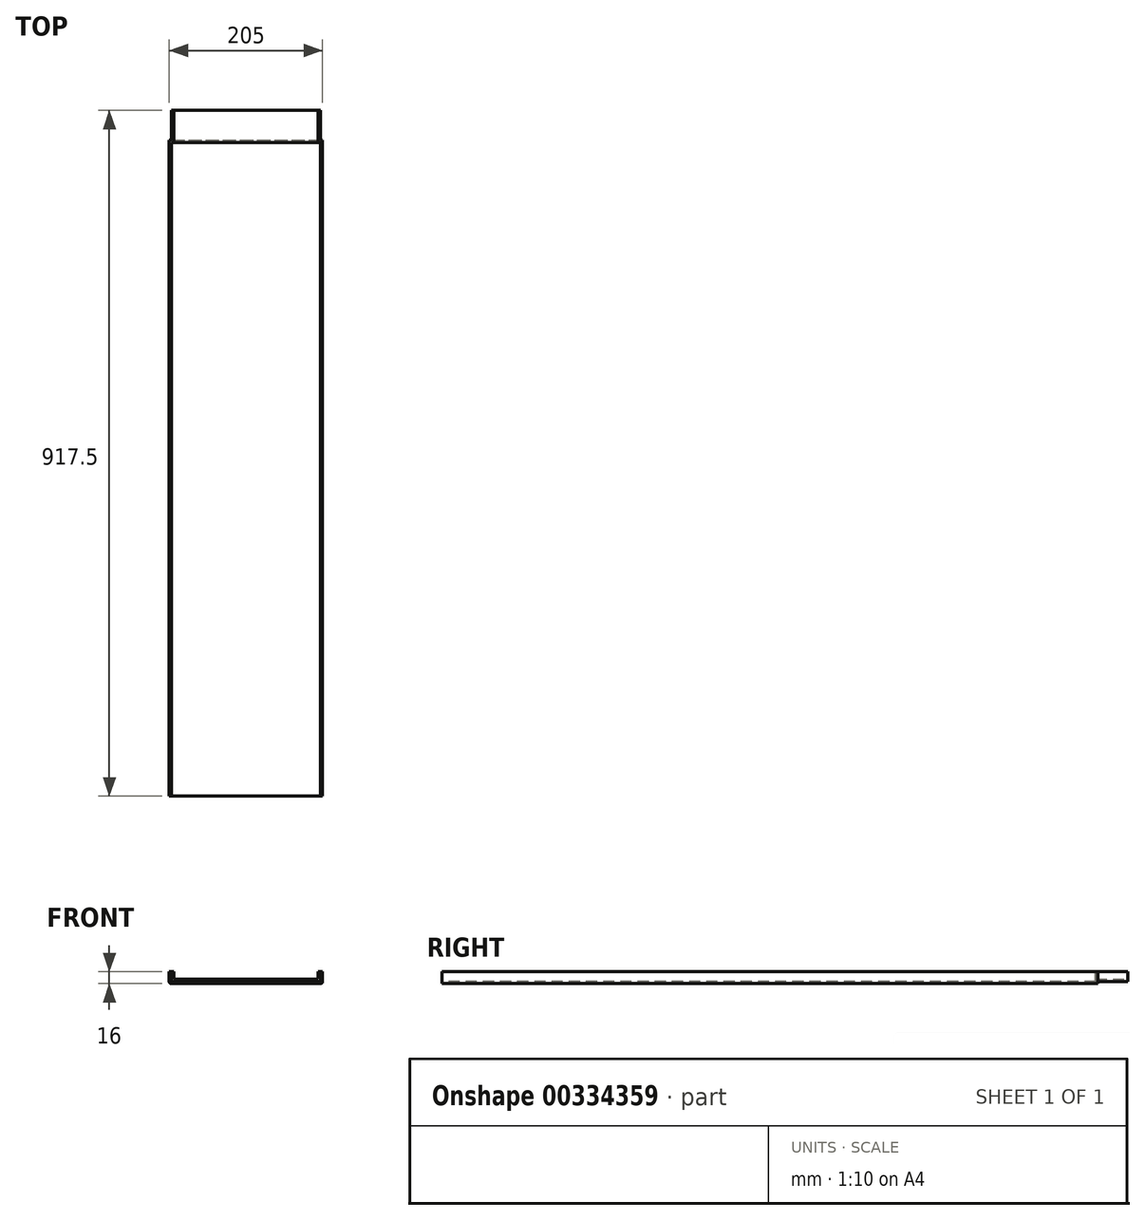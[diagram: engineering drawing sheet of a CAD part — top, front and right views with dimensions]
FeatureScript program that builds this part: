
annotation { "Feature Type Name" : "Feature", "Feature Type Description" : "" }
export const myFeature = defineFeature(function(context is Context, id is Id, definition is map)
    precondition{}
    {
        {
            var Q0;
            Q0=qCreatedBy(makeId("Front.planeOp"),FACE);
            var sketch = newSketch(context, id + "F0", { "sketchPlane" : qUnion([Q0])});
            skLineSegment(sketch, "E0.top", {"start": v(-100, -16) * mm, "end": v(100, -16) * mm});
            skLineSegment(sketch, "E0.left", {"start": v(-102.5, 16) * mm, "end": v(-102.5, -13.5) * mm});
            skLineSegment(sketch, "E0.right", {"start": v(102.5, 0) * mm, "end": v(102.5, -13.5) * mm});
            skPoint(sketch, "E0.middle", {"position": v(0, 0) * mm});
            skLineSegment(sketch, "E1.top", {"start": v(-97, -13) * mm, "end": v(97, -13) * mm});
            skLineSegment(sketch, "E1.left", {"start": v(-99.5, 13) * mm, "end": v(-99.5, -10.5) * mm});
            skLineSegment(sketch, "E1.right", {"start": v(99.5, 0) * mm, "end": v(99.5, -10.5) * mm});
            skLineSegment(sketch, "E2.top", {"start": v(-94, -10) * mm, "end": v(94, -10) * mm});
            skLineSegment(sketch, "E2.left", {"start": v(-96.5, 10) * mm, "end": v(-96.5, -7.5) * mm});
            skLineSegment(sketch, "E2.right", {"start": v(96.5, 0) * mm, "end": v(96.5, -7.5) * mm});
            skLineSegment(sketch, "E3", {"start": v(102.5, 0) * mm, "end": v(96.5, 0) * mm});
            skPoint(sketch, "E4.visualSharp", {"position": v(96.5, -10) * mm});
            skArc(sketch, "E4.filletArc", {"start": v(94, -10) * mm, "mid": v(95.77, -9.27) * mm, "end": v(96.5, -7.5) * mm});
            skPoint(sketch, "E5.visualSharp", {"position": v(99.5, -13) * mm});
            skArc(sketch, "E5.filletArc", {"start": v(97, -13) * mm, "mid": v(98.77, -12.27) * mm, "end": v(99.5, -10.5) * mm});
            skPoint(sketch, "E6.visualSharp", {"position": v(102.5, -16) * mm});
            skArc(sketch, "E6.filletArc", {"start": v(100, -16) * mm, "mid": v(101.77, -15.27) * mm, "end": v(102.5, -13.5) * mm});
            skArc(sketch, "E7.MirrorCS", {"start": v(-100, -16) * mm, "mid": v(-101.77, -15.27) * mm, "end": v(-102.5, -13.5) * mm});
            skPoint(sketch, "E8.MirrorP", {"position": v(-96.5, -10) * mm});
            skLineSegment(sketch, "E9.MirrorCS", {"start": v(96.5, -10) * mm, "end": v(-94, -10) * mm});
            skPoint(sketch, "E10.MirrorP", {"position": v(-99.5, -13) * mm});
            skArc(sketch, "E11.MirrorCS", {"start": v(-97, -13) * mm, "mid": v(-98.77, -12.27) * mm, "end": v(-99.5, -10.5) * mm});
            skArc(sketch, "E12.MirrorCS", {"start": v(-94, -10) * mm, "mid": v(-95.77, -9.27) * mm, "end": v(-96.5, -7.5) * mm});
            skPoint(sketch, "E13.MirrorP", {"position": v(-102.5, -16) * mm});
            skLineSegment(sketch, "E14.MirrorCS", {"start": v(-96.5, 0) * mm, "end": v(-96.5, -7.5) * mm});
            skLineSegment(sketch, "E15.MirrorCS", {"start": v(102.5, -16) * mm, "end": v(-100, -16) * mm});
            skLineSegment(sketch, "E16.MirrorCS", {"start": v(-102.5, 0) * mm, "end": v(-102.5, -13.5) * mm});
            skLineSegment(sketch, "E17.MirrorCS", {"start": v(99.5, -13) * mm, "end": v(-97, -13) * mm});
            skLineSegment(sketch, "E18.MirrorCS", {"start": v(-99.5, 0) * mm, "end": v(-99.5, -10.5) * mm});
            skPoint(sketch, "E0.bottom.end.orphan", {"position": v(102.5, 16) * mm});
            skPoint(sketch, "E1.bottom.end.orphan", {"position": v(99.5, 13) * mm});
            skPoint(sketch, "E2.bottom.end.orphan", {"position": v(96.5, 10) * mm});
            skLineSegment(sketch, "E19.trimOffspring", {"start": v(-96.5, 0) * mm, "end": v(-102.5, 0) * mm});
            skPoint(sketch, "E20.orphan", {"position": v(-102.5, 16) * mm});
            skPoint(sketch, "E21.orphan", {"position": v(-99.5, 13) * mm});
            skPoint(sketch, "E22.orphan", {"position": v(-96.5, 10) * mm});
            skSolve(sketch);
        }
        {
            var Q0;
            Q0=qSketchRegion(id+"F0",true);
            extrude(context, id + "F1", {"entities" : qUnion([Q0]), "depth" : 917.5 * mm});
        }
        {
            var Q0;
            {var subQ6=sQuery(id+"F0.wireOp",EDGE,"E0.right");Q0=makeQuery(id+"F0.imprint","IMPRINT",FACE,{"disambiguationData":[TD([[makeQuery(id+"F0.imprint","IMPRINT",EDGE,{"derivedFrom":subQ6}),-1.0]])]});}
            extrude(context, id + "F2", {"entities" : qUnion([Q0]), "operationType" : NewBodyOperationType.REMOVE, "depth" : 40 * mm});
        }
        {
            var Q0;
            Q0=makeQuery(id+"F1.opExtrude","SWEPT_FACE",FACE,{"disambiguationData":[OSD([sQuery(id+"F0.wireOp",EDGE,"E19.trimOffspring")])]});
            var sketch = newSketch(context, id + "F3", { "sketchPlane" : qUnion([Q0])});
            skLineSegment(sketch, "E23.bottom", {"start": v(-99.5, -43) * mm, "end": v(99.5, -43) * mm});
            skLineSegment(sketch, "E23.top", {"start": v(-99.5, -813.79) * mm, "end": v(99.5, -813.79) * mm});
            skLineSegment(sketch, "E23.left", {"start": v(-99.5, -43) * mm, "end": v(-99.5, -813.79) * mm});
            skLineSegment(sketch, "E23.right", {"start": v(99.5, -43) * mm, "end": v(99.5, -813.79) * mm});
            skSolve(sketch);
        }
        {
            var Q0;
            Q0 = qSketchRegion(id + "F3", true);
            extrude(context, id + "F4", {"entities" : qUnion([Q0]), "operationType" : NewBodyOperationType.REMOVE, "oppositeDirection" : true, "depth" : 13 * mm});
        }
        {
            var Q0;
            Q0=makeQuery(id+"F4.boolean.opBoolean","COPY",FACE,{"derivedFrom":makeQuery(id+"F4.opExtrude","SWEPT_FACE",FACE,{"disambiguationData":[OSD([sQuery(id+"F3.wireOp",EDGE,"E23.top")])]})});
            extrude(context, id + "F5", {"entities" : qUnion([Q0]), "operationType" : NewBodyOperationType.REMOVE, "oppositeDirection" : true, "depth" : 110 * mm});
        }
    });
